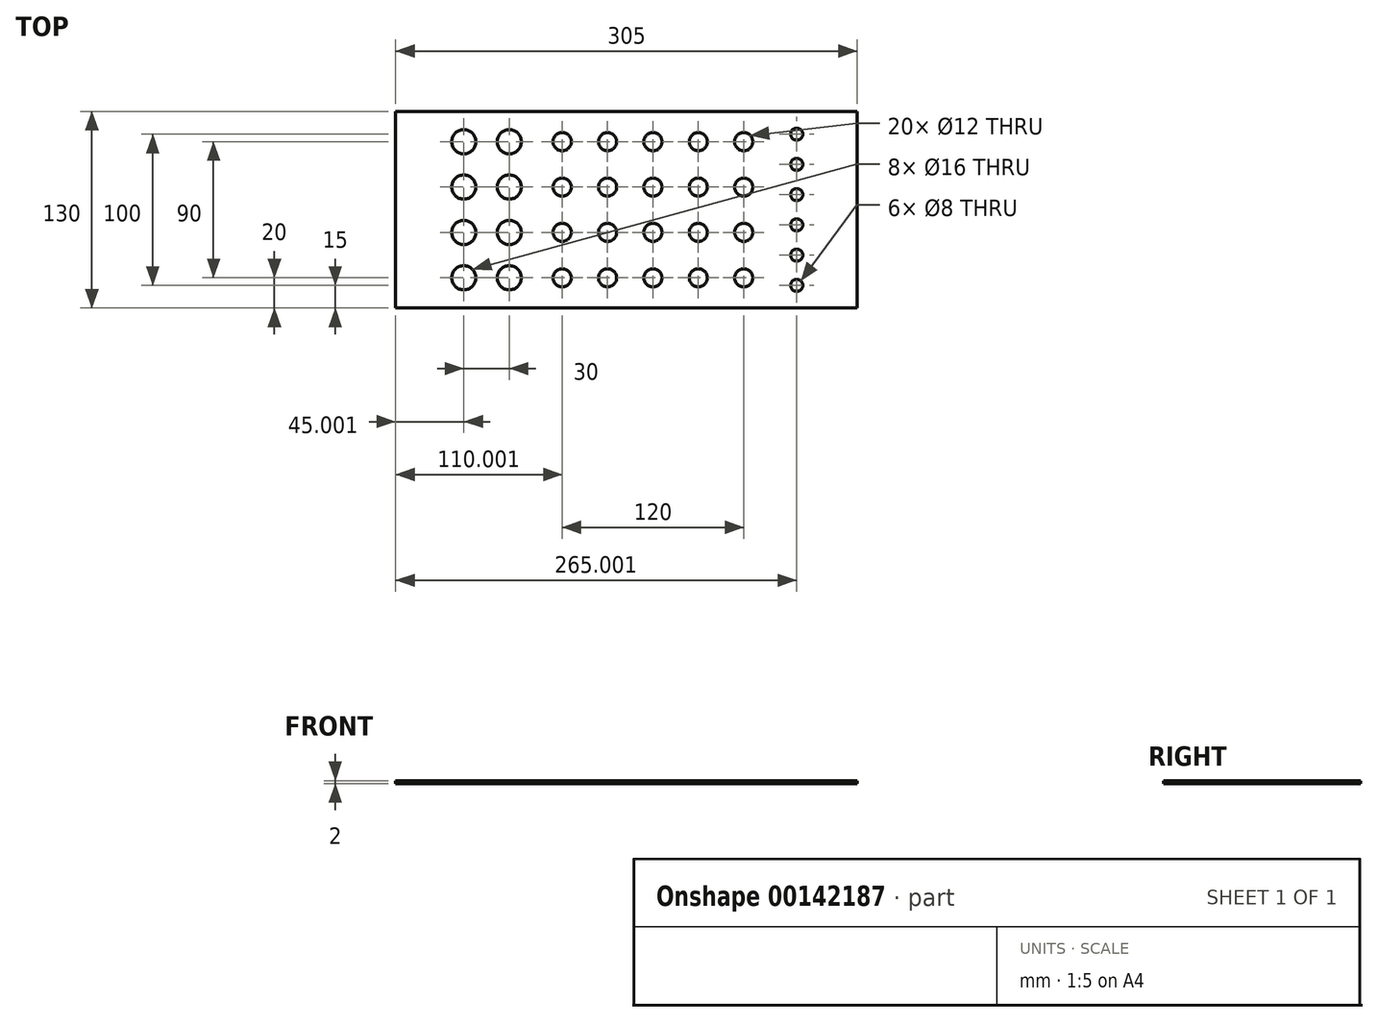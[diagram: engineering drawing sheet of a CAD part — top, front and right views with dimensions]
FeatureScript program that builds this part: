
annotation { "Feature Type Name" : "Feature", "Feature Type Description" : "" }
export const myFeature = defineFeature(function(context is Context, id is Id, definition is map)
    precondition{}
    {
        {
            var Q0;
            Q0=qCreatedBy(makeId("Top.planeOp"),FACE);
            var sketch = newSketch(context, id + "F0", { "sketchPlane" : qUnion([Q0])});
            skLineSegment(sketch, "E0.bottom", {"start": v(-162.42, -46.34) * mm, "end": v(142.58, -46.34) * mm});
            skLineSegment(sketch, "E0.top", {"start": v(-162.42, 83.66) * mm, "end": v(142.58, 83.66) * mm});
            skLineSegment(sketch, "E0.left", {"start": v(-162.42, -46.34) * mm, "end": v(-162.42, 83.66) * mm});
            skLineSegment(sketch, "E0.right", {"start": v(142.58, -46.34) * mm, "end": v(142.58, 83.66) * mm});
            skLineSegment(sketch, "E1", {"start": v(-137.42, 83.66) * mm, "end": v(-137.42, -46.34) * mm, "construction": true});
            skLineSegment(sketch, "E2", {"start": v(117.58, 83.66) * mm, "end": v(117.58, -46.34) * mm, "construction": true});
            skLineSegment(sketch, "E3", {"start": v(-137.42, -36.34) * mm, "end": v(117.58, -36.34) * mm, "construction": true});
            skCircle(sketch, "E4", {"center": v(102.58, 68.66) * mm, "radius": 4 * mm});
            skCircle(sketch, "E5.0.1.0", {"center": v(102.58, 48.66) * mm, "radius": 4 * mm});
            skCircle(sketch, "E5.0.2.0", {"center": v(102.58, 28.66) * mm, "radius": 4 * mm});
            skCircle(sketch, "E5.0.3.0", {"center": v(102.58, 8.66) * mm, "radius": 4 * mm});
            skCircle(sketch, "E5.0.4.0", {"center": v(102.58, -11.34) * mm, "radius": 4 * mm});
            skCircle(sketch, "E5.0.5.0", {"center": v(102.58, -31.34) * mm, "radius": 4 * mm});
            skLineSegment(sketch, "E5.direction1", {"start": v(102.58, 68.66) * mm, "end": v(127.58, 68.66) * mm, "construction": true});
            skLineSegment(sketch, "E5.direction2", {"start": v(102.58, 68.66) * mm, "end": v(102.58, 48.66) * mm, "construction": true});
            skCircle(sketch, "E6", {"center": v(67.58, 63.66) * mm, "radius": 6 * mm});
            skCircle(sketch, "E7.0.1.0", {"center": v(67.58, 33.66) * mm, "radius": 6 * mm});
            skCircle(sketch, "E7.0.2.0", {"center": v(67.58, 3.66) * mm, "radius": 6 * mm});
            skCircle(sketch, "E7.0.3.0", {"center": v(67.58, -26.34) * mm, "radius": 6 * mm});
            skCircle(sketch, "E7.1.0.0", {"center": v(37.58, 63.66) * mm, "radius": 6 * mm});
            skCircle(sketch, "E7.1.1.0", {"center": v(37.58, 33.66) * mm, "radius": 6 * mm});
            skCircle(sketch, "E7.1.2.0", {"center": v(37.58, 3.66) * mm, "radius": 6 * mm});
            skCircle(sketch, "E7.1.3.0", {"center": v(37.58, -26.34) * mm, "radius": 6 * mm});
            skCircle(sketch, "E7.2.0.0", {"center": v(7.58, 63.66) * mm, "radius": 6 * mm});
            skCircle(sketch, "E7.2.1.0", {"center": v(7.58, 33.66) * mm, "radius": 6 * mm});
            skCircle(sketch, "E7.2.2.0", {"center": v(7.58, 3.66) * mm, "radius": 6 * mm});
            skCircle(sketch, "E7.2.3.0", {"center": v(7.58, -26.34) * mm, "radius": 6 * mm});
            skLineSegment(sketch, "E7.direction1", {"start": v(67.58, 63.66) * mm, "end": v(37.58, 63.66) * mm, "construction": true});
            skLineSegment(sketch, "E7.direction2", {"start": v(67.58, 63.66) * mm, "end": v(67.58, 33.66) * mm, "construction": true});
            skCircle(sketch, "E8.0.3.0", {"center": v(-22.42, 63.66) * mm, "radius": 6 * mm});
            skCircle(sketch, "E8.0.3.1", {"center": v(-22.42, 33.66) * mm, "radius": 6 * mm});
            skCircle(sketch, "E8.0.3.2", {"center": v(-22.42, 3.66) * mm, "radius": 6 * mm});
            skCircle(sketch, "E8.0.3.3", {"center": v(-22.42, -26.34) * mm, "radius": 6 * mm});
            skCircle(sketch, "E9.0.4.0", {"center": v(-52.42, 63.66) * mm, "radius": 6 * mm});
            skCircle(sketch, "E9.0.4.1", {"center": v(-52.42, 33.66) * mm, "radius": 6 * mm});
            skCircle(sketch, "E9.0.4.2", {"center": v(-52.42, 3.66) * mm, "radius": 6 * mm});
            skCircle(sketch, "E9.0.4.3", {"center": v(-52.42, -26.34) * mm, "radius": 6 * mm});
            skCircle(sketch, "E10", {"center": v(-87.42, 63.66) * mm, "radius": 8 * mm});
            skCircle(sketch, "E11.0.1.0", {"center": v(-87.42, 33.66) * mm, "radius": 8 * mm});
            skCircle(sketch, "E11.0.2.0", {"center": v(-87.42, 3.66) * mm, "radius": 8 * mm});
            skCircle(sketch, "E11.0.3.0", {"center": v(-87.42, -26.34) * mm, "radius": 8 * mm});
            skCircle(sketch, "E11.1.0.0", {"center": v(-117.42, 63.66) * mm, "radius": 8 * mm});
            skCircle(sketch, "E11.1.1.0", {"center": v(-117.42, 33.66) * mm, "radius": 8 * mm});
            skCircle(sketch, "E11.1.2.0", {"center": v(-117.42, 3.66) * mm, "radius": 8 * mm});
            skCircle(sketch, "E11.1.3.0", {"center": v(-117.42, -26.34) * mm, "radius": 8 * mm});
            skLineSegment(sketch, "E11.direction1", {"start": v(-87.42, 63.66) * mm, "end": v(-117.42, 63.66) * mm, "construction": true});
            skLineSegment(sketch, "E11.direction2", {"start": v(-87.42, 63.66) * mm, "end": v(-87.42, 33.66) * mm, "construction": true});
            skSolve(sketch);
        }
        {
            var Q0;
            Q0=makeQuery(id+"F0.imprint","IMPRINT",FACE,{"disambiguationData":[TD([[makeQuery(id+"F0.imprint","IMPRINT",EDGE,{"derivedFrom":sQuery(id+"F0.wireOp",EDGE,"E0.bottom")}),1.0]])]});
            extrude(context, id + "F1", {"entities" : qUnion([Q0]), "depth" : 2 * mm});
        }
    });
